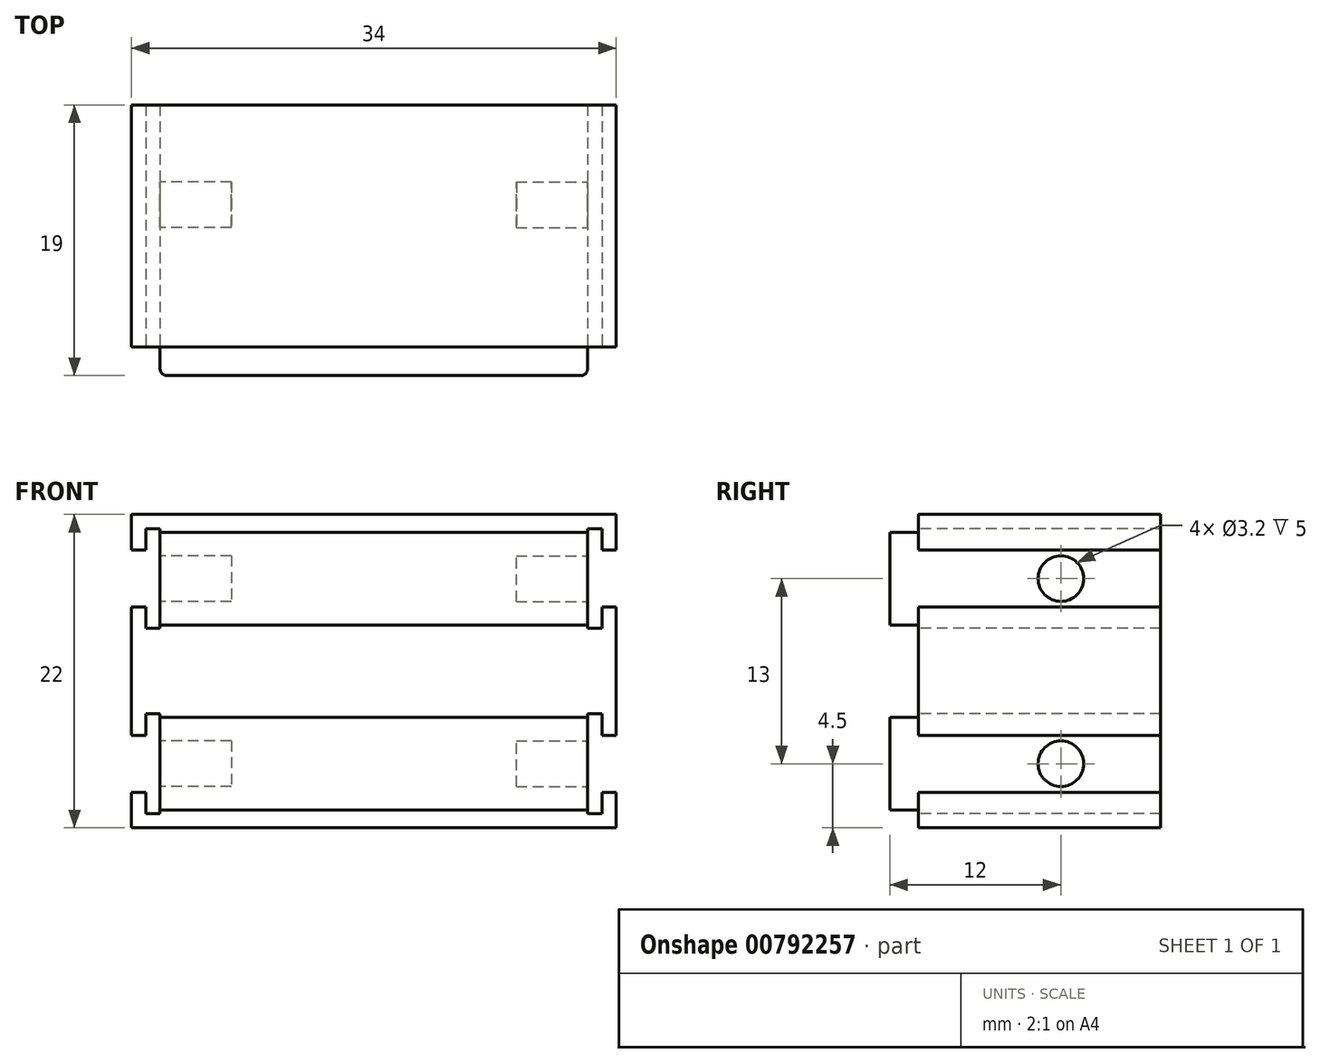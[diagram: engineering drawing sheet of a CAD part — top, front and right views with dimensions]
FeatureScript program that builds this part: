
annotation { "Feature Type Name" : "Feature", "Feature Type Description" : "" }
export const myFeature = defineFeature(function(context is Context, id is Id, definition is map)
    precondition{}
    {
        {
            var Q0;
            Q0=qCreatedBy(makeId("Front.planeOp"),FACE);
            var sketch = newSketch(context, id + "F0", { "sketchPlane" : qUnion([Q0])});
            skLineSegment(sketch, "E0.bottom", {"start": v(17, -11) * mm, "end": v(-17, -11) * mm});
            skLineSegment(sketch, "E0.top", {"start": v(17, 11) * mm, "end": v(-17, 11) * mm});
            skLineSegment(sketch, "E0.left", {"start": v(17, -11) * mm, "end": v(17, 11) * mm});
            skLineSegment(sketch, "E0.right", {"start": v(-17, -11) * mm, "end": v(-17, 11) * mm});
            skPoint(sketch, "E0.middle", {"position": v(0, 0) * mm});
            skSolve(sketch);
        }
        {
            var Q0;
            Q0 = qSketchRegion(id + "F0", true);
            extrude(context, id + "F1", {"entities" : qUnion([Q0]), "oppositeDirection" : true, "depth" : 17 * mm, "offsetDistance" : 25 * mm});
        }
        {
            var Q0;
            Q0=makeQuery(id+"F1.opExtrude","CAP_FACE",FACE,{"disambiguationData":[OSD([sQuery(id+"F0.wireOp",EDGE,"E0.bottom"),sQuery(id+"F0.wireOp",EDGE,"E0.top"),sQuery(id+"F0.wireOp",EDGE,"E0.left"),sQuery(id+"F0.wireOp",EDGE,"E0.right")])],"isStart":true});
            var sketch = newSketch(context, id + "F2", { "sketchPlane" : qUnion([Q0])});
            skLineSegment(sketch, "E1", {"start": v(-17, 8.5) * mm, "end": v(-16, 8.5) * mm});
            skLineSegment(sketch, "E2", {"start": v(-16, 8.5) * mm, "end": v(-16, 10) * mm});
            skLineSegment(sketch, "E3", {"start": v(-16, 10) * mm, "end": v(-15, 10) * mm});
            skLineSegment(sketch, "E4", {"start": v(-15, 10) * mm, "end": v(-15, 3) * mm});
            skLineSegment(sketch, "E5", {"start": v(-15, 3) * mm, "end": v(-16, 3) * mm});
            skLineSegment(sketch, "E6", {"start": v(-16, 3) * mm, "end": v(-16, 4.5) * mm});
            skLineSegment(sketch, "E7", {"start": v(-16, 4.5) * mm, "end": v(-17, 4.5) * mm});
            skLineSegment(sketch, "E8", {"start": v(-17, 4.5) * mm, "end": v(-17, 8.5) * mm});
            skLineSegment(sketch, "E9", {"start": v(-17, 0) * mm, "end": v(17, 0) * mm, "construction": true});
            skLineSegment(sketch, "E10", {"start": v(0, 11) * mm, "end": v(0, -11) * mm, "construction": true});
            skLineSegment(sketch, "E11.MirrorCS", {"start": v(15, 3) * mm, "end": v(16, 3) * mm});
            skLineSegment(sketch, "E12.MirrorCS", {"start": v(17, 8.5) * mm, "end": v(16, 8.5) * mm});
            skLineSegment(sketch, "E13.MirrorCS", {"start": v(16, 8.5) * mm, "end": v(16, 10) * mm});
            skLineSegment(sketch, "E14.MirrorCS", {"start": v(17, 4.5) * mm, "end": v(17, 8.5) * mm});
            skLineSegment(sketch, "E15.MirrorCS", {"start": v(16, 10) * mm, "end": v(15, 10) * mm});
            skLineSegment(sketch, "E16.MirrorCS", {"start": v(15, 10) * mm, "end": v(15, 3) * mm});
            skLineSegment(sketch, "E17.MirrorCS", {"start": v(16, 3) * mm, "end": v(16, 4.5) * mm});
            skLineSegment(sketch, "E18.MirrorCS", {"start": v(16, 4.5) * mm, "end": v(17, 4.5) * mm});
            skLineSegment(sketch, "E19.MirrorCS", {"start": v(16, -4.5) * mm, "end": v(17, -4.5) * mm});
            skLineSegment(sketch, "E20.MirrorCS", {"start": v(17, -8.5) * mm, "end": v(16, -8.5) * mm});
            skLineSegment(sketch, "E21.MirrorCS", {"start": v(15, -3) * mm, "end": v(16, -3) * mm});
            skLineSegment(sketch, "E22.MirrorCS", {"start": v(16, -10) * mm, "end": v(15, -10) * mm});
            skLineSegment(sketch, "E23.MirrorCS", {"start": v(-17, -8.5) * mm, "end": v(-16, -8.5) * mm});
            skLineSegment(sketch, "E24.MirrorCS", {"start": v(-16, -10) * mm, "end": v(-15, -10) * mm});
            skLineSegment(sketch, "E25.MirrorCS", {"start": v(-16, -4.5) * mm, "end": v(-17, -4.5) * mm});
            skLineSegment(sketch, "E26.MirrorCS", {"start": v(-15, -3) * mm, "end": v(-16, -3) * mm});
            skLineSegment(sketch, "E27.MirrorCS", {"start": v(16, -3) * mm, "end": v(16, -4.5) * mm});
            skLineSegment(sketch, "E28.MirrorCS", {"start": v(16, -8.5) * mm, "end": v(16, -10) * mm});
            skLineSegment(sketch, "E29.MirrorCS", {"start": v(17, -4.5) * mm, "end": v(17, -8.5) * mm});
            skLineSegment(sketch, "E30.MirrorCS", {"start": v(-17, -4.5) * mm, "end": v(-17, -8.5) * mm});
            skLineSegment(sketch, "E31.MirrorCS", {"start": v(15, -10) * mm, "end": v(15, -3) * mm});
            skLineSegment(sketch, "E32.MirrorCS", {"start": v(-16, -8.5) * mm, "end": v(-16, -10) * mm});
            skLineSegment(sketch, "E33.MirrorCS", {"start": v(-15, -10) * mm, "end": v(-15, -3) * mm});
            skLineSegment(sketch, "E34.MirrorCS", {"start": v(-16, -3) * mm, "end": v(-16, -4.5) * mm});
            skSolve(sketch);
        }
        {
            var Q0;
            Q0 = qSketchRegion(id + "F2", true);
            extrude(context, id + "F3", {"entities" : qUnion([Q0]), "operationType" : NewBodyOperationType.REMOVE, "endBound" : BoundingType.THROUGH_ALL, "oppositeDirection" : true, "depth" : 25 * mm, "offsetDistance" : 25 * mm});
        }
        {
            var Q0;
            Q0=makeQuery(id+"F1.opExtrude","CAP_FACE",FACE,{"disambiguationData":[OSD([sQuery(id+"F0.wireOp",EDGE,"E0.bottom"),sQuery(id+"F0.wireOp",EDGE,"E0.top"),sQuery(id+"F0.wireOp",EDGE,"E0.left"),sQuery(id+"F0.wireOp",EDGE,"E0.right")])],"isStart":true});
            var sketch = newSketch(context, id + "F4", { "sketchPlane" : qUnion([Q0])});
            skLineSegment(sketch, "E35", {"start": v(-15, 3) * mm, "end": v(15, 3) * mm, "construction": true});
            skLineSegment(sketch, "E36", {"start": v(-15, -3) * mm, "end": v(15, -3) * mm, "construction": true});
            skLineSegment(sketch, "E37.bottom", {"start": v(-15, 9.75) * mm, "end": v(15, 9.75) * mm});
            skLineSegment(sketch, "E37.top", {"start": v(-15, 3.25) * mm, "end": v(15, 3.25) * mm});
            skLineSegment(sketch, "E37.left", {"start": v(-15, 9.75) * mm, "end": v(-15, 3.25) * mm});
            skLineSegment(sketch, "E37.right", {"start": v(15, 9.75) * mm, "end": v(15, 3.25) * mm});
            skLineSegment(sketch, "E38.bottom", {"start": v(-15, -3.25) * mm, "end": v(15, -3.25) * mm});
            skLineSegment(sketch, "E38.top", {"start": v(-15, -9.75) * mm, "end": v(15, -9.75) * mm});
            skLineSegment(sketch, "E38.left", {"start": v(-15, -3.25) * mm, "end": v(-15, -9.75) * mm});
            skLineSegment(sketch, "E38.right", {"start": v(15, -3.25) * mm, "end": v(15, -9.75) * mm});
            skSolve(sketch);
        }
        {
            var Q0;
            Q0 = qSketchRegion(id + "F4", true);
            extrude(context, id + "F5", {"entities" : qUnion([Q0]), "operationType" : NewBodyOperationType.ADD, "depth" : 2 * mm, "offsetDistance" : 25 * mm});
        }
        {
            var Q0;
            Q0=makeQuery(id+"F5.boolean.opBoolean","MERGE",FACE,{"derivedFrom":[makeQuery(id+"F3.boolean.opBoolean","COPY",FACE,{"derivedFrom":makeQuery(id+"F3.opExtrude","SWEPT_FACE",FACE,{"disambiguationData":[OSD([sQuery(id+"F2.wireOp",EDGE,"E4")])]})}),makeQuery(id+"F5.opExtrude","SWEPT_FACE",FACE,{"disambiguationData":[OSD([sQuery(id+"F4.wireOp",EDGE,"E37.left")])]})]});
            cPlane(context, id + "F6", {"entities" : qUnion([Q0]), "cplaneType" : CPlaneType.OFFSET, "offset" : 0 * mm, "width" : 150 * mm, "height" : 150 * mm});
        }
        {
            var Q0;
            Q0=qCreatedBy(id+"F6.planeOp",FACE);
            var sketch = newSketch(context, id + "F7", { "sketchPlane" : qUnion([Q0])});
            skCircle(sketch, "E39", {"center": v(-10, 6.5) * mm, "radius": 1.6 * mm});
            skCircle(sketch, "E40", {"center": v(-10, -6.5) * mm, "radius": 1.6 * mm});
            skSolve(sketch);
        }
        {
            var Q0;
            Q0 = qSketchRegion(id + "F7", true);
            extrude(context, id + "F8", {"entities" : qUnion([Q0]), "operationType" : NewBodyOperationType.REMOVE, "oppositeDirection" : true, "depth" : 5 * mm, "offsetDistance" : 25 * mm});
        }
        {
            var Q0;
            Q0=makeQuery(id+"F5.boolean.opBoolean","MERGE",FACE,{"derivedFrom":[makeQuery(id+"F3.boolean.opBoolean","COPY",FACE,{"derivedFrom":makeQuery(id+"F3.opExtrude","SWEPT_FACE",FACE,{"disambiguationData":[OSD([sQuery(id+"F2.wireOp",EDGE,"E16.MirrorCS")])]})}),makeQuery(id+"F5.opExtrude","SWEPT_FACE",FACE,{"disambiguationData":[OSD([sQuery(id+"F4.wireOp",EDGE,"E37.right")])]})]});
            cPlane(context, id + "F9", {"entities" : qUnion([Q0]), "cplaneType" : CPlaneType.OFFSET, "offset" : 0 * mm, "width" : 150 * mm, "height" : 150 * mm});
        }
        {
            var Q0;
            Q0=qCreatedBy(id+"F9.planeOp",FACE);
            var sketch = newSketch(context, id + "F10", { "sketchPlane" : qUnion([Q0])});
            skCircle(sketch, "E41", {"center": v(10, 6.5) * mm, "radius": 1.6 * mm});
            skCircle(sketch, "E42", {"center": v(10, -6.5) * mm, "radius": 1.6 * mm});
            skSolve(sketch);
        }
        {
            var Q0;
            Q0 = qSketchRegion(id + "F10", true);
            extrude(context, id + "F11", {"entities" : qUnion([Q0]), "operationType" : NewBodyOperationType.REMOVE, "oppositeDirection" : true, "depth" : 5 * mm, "offsetDistance" : 25 * mm});
        }
        {
            var Q0;
            Q0=makeQuery(id+"F5.opExtrude","CAP_EDGE",EDGE,{"disambiguationData":[OSD([sQuery(id+"F4.wireOp",EDGE,"E37.right")])],"isStart":false});
            var Q1;
            Q1=makeQuery(id+"F5.opExtrude","CAP_EDGE",EDGE,{"disambiguationData":[OSD([sQuery(id+"F4.wireOp",EDGE,"E37.left")])],"isStart":false});
            var Q2;
            Q2=makeQuery(id+"F5.opExtrude","CAP_EDGE",EDGE,{"disambiguationData":[OSD([sQuery(id+"F4.wireOp",EDGE,"E38.right")])],"isStart":false});
            var Q3;
            Q3=makeQuery(id+"F5.opExtrude","CAP_EDGE",EDGE,{"disambiguationData":[OSD([sQuery(id+"F4.wireOp",EDGE,"E38.left")])],"isStart":false});
            fillet(context, id + "F12", {"entities" : qUnion([Q0, Q1, Q2, Q3]), "radius" : 0.5 * mm, "tangentPropagation" : true, "allowEdgeOverflow" : false});
        }
    });
